# Revit family: 844N070MS
name_source: partatom
category: Lighting Fixtures
revit_build: Autodesk Revit 2014 (Build: 20130308_1515(x64)
units: mm (PartAtom-declared; Revit-internal decimal feet)

## types (1)
- 844N/070/MS
    Apparent Load = 70 VA
    Assembly Code = D5020200
    Color Filter = 16777215
    Connector Description = Lighting Connector
    Default Elevation = 1219.2 mm  [stored 4 ft]
    Description = The 800 series is a range of stainless steel asymmetrical floodlights. These floods are designed for optimum light output and efficiency to ensure the minimum number of luminaires is required.Its suitable for low temperature applications (-40°C).

Photometrically superior asymmetric reflector.
Marine grade stainless steel body and toughened glass cover.
Suspended cover front.
Standard control gear for use with IEC lamps.
The 800 series is a premium range of stainless steel bodied asymmetrical beam floodlights suitable for tubular HPS and metal halide lamps from 70W to 400W and also 500W tungsten-halogen. Click the 'Contact Us' link above to get in touch with us and discuss how the 800 series range could work
    Dimming Lamp Color Temperature Shift = <None>
    Emit Shape Visible in Rendering = No
    Emit from Rectangle Length = 300 mm
    Emit from Rectangle Width = 328 mm  [stored 1.07612 ft]
    Features = Photometrically superior
asymmetric reflector
Marine grade stainless steel body
and toughened glass cover
Quick release fasteners
for ease of relamping
and maintenance
Suspended cover front
Suitable for low temperature
applications (-40°C)
Standard control gear for use
with IEC lamps
    Fixture distribution = Direct
    Glass = Hubbell - Glass
    Height = 443 mm  [stored 1.45341 ft]
    Housing Material = Paint - Hubbell - Textured Camera Black
    IP Rating = IP66/67
    Lamp = LED
    Length = 348 mm  [stored 1.14173 ft]
    Load Classification = Lighting
    Manufacturer = Chalmit
    Model = 844N/070/MS
    Mounting = Paint - Hubbell - Light Silver
    Photometric Web File = CHL_844N_070_MS HPS.ies
    Power Factor = 1
    Product Documentation Link = https://hubbellcdn.com
    Product Link = https://www.hubbell.com
    Reflector Finish = Hubbell - White Glass
    Tilt Angle = -30.00°
    URL = https://www.hubbell.com
    Voltage = 120 V
    Warranty = 5 years Warranty
    Wattage Comments = 70W
    Watts = 70 W
    Width = 150 mm
    Wings = Paint - Hubbell - Light Silver

note: [stored X ft] marks values corroborated as IEEE doubles in the binary element streams (Revit-internal decimal feet)

## geometry (parser evidence)
native form markers: Sweep x4
no freeform markers — native parametric forms only
